# Revit family: Chair-Multi_Purpose-Allermuir-Kojak-A832
name_source: partatom
category: Furniture
revit_build: Autodesk Revit Architecture 2012 (Build: 20110309_2315(x64)
units: mm (PartAtom-declared; Revit-internal decimal feet)

## types (1)
- A832
    04 CSI = 12 51 00
    95 CSI = 12510
    Assembly Code = E2020200
    Base = Fabric - Allermuir - Upholstery - Pebbled - Chrome - Satin
    Brochure URL = http://www.allermuir.net
    CAD Blocks URL = http://www.allermuir.net
    Color Availability = See price list for material options
    Description = High stool, no arms
    Fabric Spec Sheets = http://www.allermuir.net
    Glides = Plastic - Allermuir - Smooth Black
    LEED Stats URL = http://www.allermuir.net
    Manufacturer = Allermuir
    Manufacturer Fax = (419) 887 5805
    Model = A832
    Optional Feature Notes = Polished Chrome footrest
    Overall Depth = 20.5 "
    Overall Height = 43 "
    Overall Width = 18 "
    Plastic Arms in Black = No
    Plastic glides = Yes
    Plugin Data URL = http://products.ecoscorecard.com
    Pricing URL = http://www.allermuir.net
    Product Line = Kojak
    Product Page URL = http://www.allermuir.net
    Seat Depth = 17 "
    Seat Height = 29.5 "
    Seat Width = 16.5 "
    Seat or Top = Fabric - Allermuir - Upholstery - Pebbled - Smooth - Dark Gray
    Specifications URL = http://www.allermuir.net
    Stacks = No
    Subcategory = Multi-Purpose Line
    Tubular Steel Legs = Yes
    URL = http://www.allermuir.net
    Upholstered Seat = No
    Weight = 25.00 lb
    ecoScorecard Product Page = http://products.ecoscorecard.com
    ecoScorecard_data = http://thesenatorgroup.ecoscorecard.com

## geometry (parser evidence)
native form markers: Blend x12, Sweep x4
no freeform markers — native parametric forms only
